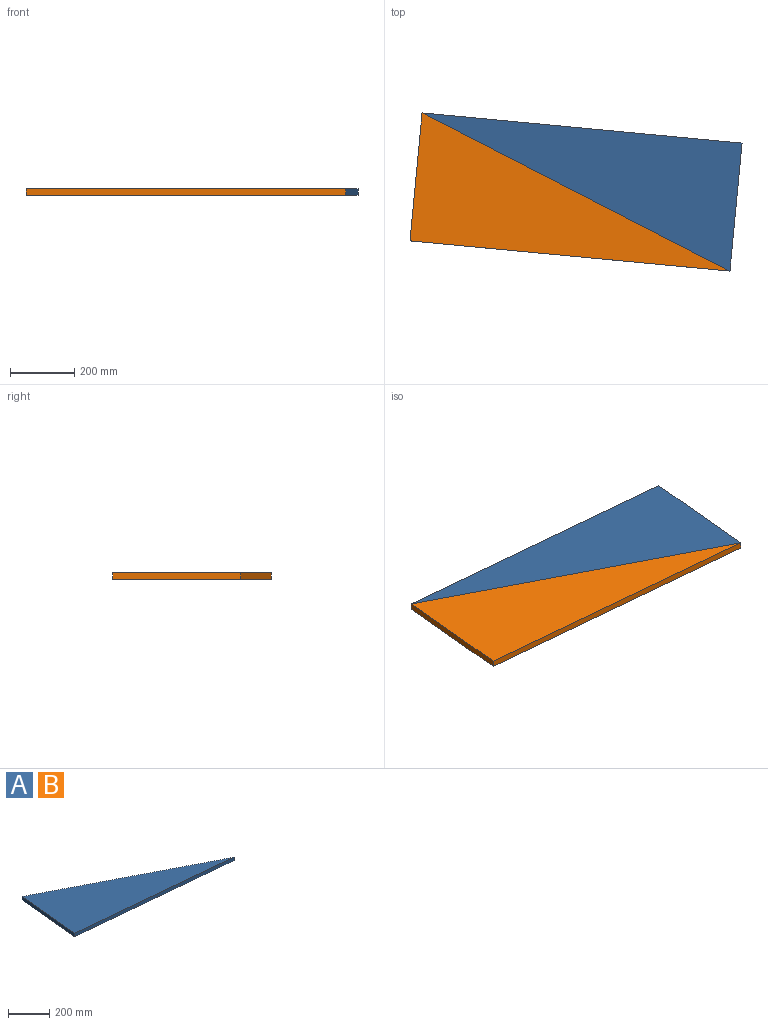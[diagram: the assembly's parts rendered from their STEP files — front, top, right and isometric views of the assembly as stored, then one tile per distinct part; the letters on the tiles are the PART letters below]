
ASSEMBLY  parts=2 mates=1
PART A: 5 faces, bbox 995.6x492.1x20 mm
  f0: plane 398.23x37.54mm, normal (-1,0.09,0), area 8000mm2, adj f1,f2,f3,f4
  f1: plane 995.59x93.86mm, normal (-0.09,-1,0), area 20000mm2, adj f0,f2,f3,f4
  f2: plane 958.04x492.09mm, normal (0.46,0.89,0), area 21540.7mm2, adj f0,f1,f3,f4
  f3: plane 995.59x492.09mm, normal (0,0,1), area 200000mm2, adj f0,f1,f2
  f4: plane 995.59x492.09mm, normal (0,0,-1), area 200000mm2, adj f0,f1,f2
PART B: same geometry as A
PLACE A rot(axis=(0,0,-1),180deg) t=(15.64,329.18,-18.83)mm
PLACE B t=(-8.47,403.11,-18.83)mm
MATE fastened B.f2 <-> A.f2  axis (0.46,0.89,0) through (3.59,366.14,-8.83)mm
